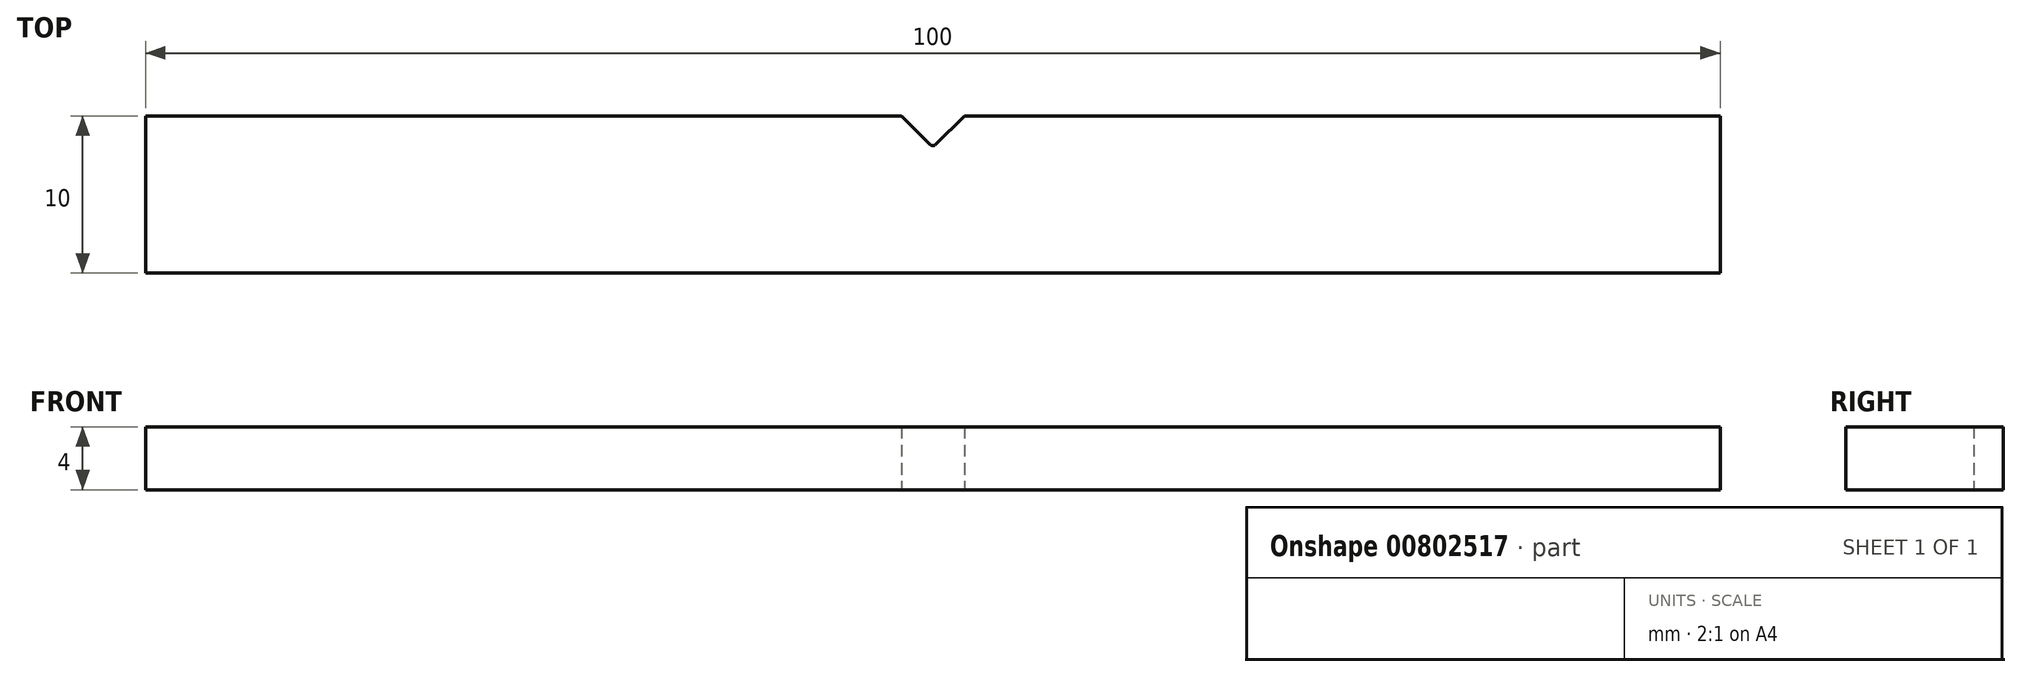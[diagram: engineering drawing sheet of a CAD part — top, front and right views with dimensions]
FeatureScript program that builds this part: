
annotation { "Feature Type Name" : "Feature", "Feature Type Description" : "" }
export const myFeature = defineFeature(function(context is Context, id is Id, definition is map)
    precondition{}
    {
        {
            var Q0;
            Q0=qCreatedBy(makeId("Top.planeOp"),FACE);
            var sketch = newSketch(context, id + "F0", { "sketchPlane" : qUnion([Q0])});
            skLineSegment(sketch, "E0.bottom", {"start": v(0, 0) * mm, "end": v(100, 0) * mm});
            skLineSegment(sketch, "E0.top", {"start": v(0, 10) * mm, "end": v(48, 10) * mm});
            skLineSegment(sketch, "E0.left", {"start": v(0, 0) * mm, "end": v(0, 10) * mm});
            skLineSegment(sketch, "E0.right", {"start": v(100, 0) * mm, "end": v(100, 10) * mm});
            skLineSegment(sketch, "E1", {"start": v(50, 10) * mm, "end": v(50, 0) * mm, "construction": true});
            skLineSegment(sketch, "E2", {"start": v(48, 10) * mm, "end": v(49.82, 8.18) * mm});
            skLineSegment(sketch, "E3", {"start": v(50.18, 8.18) * mm, "end": v(52, 10) * mm});
            skPoint(sketch, "E4.visualSharp", {"position": v(50, 8) * mm});
            skArc(sketch, "E4.filletArc", {"start": v(49.82, 8.18) * mm, "mid": v(50, 8.1) * mm, "end": v(50.18, 8.18) * mm});
            skLineSegment(sketch, "E5.trimOffspring", {"start": v(52, 10) * mm, "end": v(100, 10) * mm});
            skSolve(sketch);
        }
        {
            var Q0;
            Q0 = qSketchRegion(id + "F0", true);
            extrude(context, id + "F1", {"entities" : qUnion([Q0]), "depth" : 4 * mm, "offsetDistance" : 25 * mm});
        }
    });
